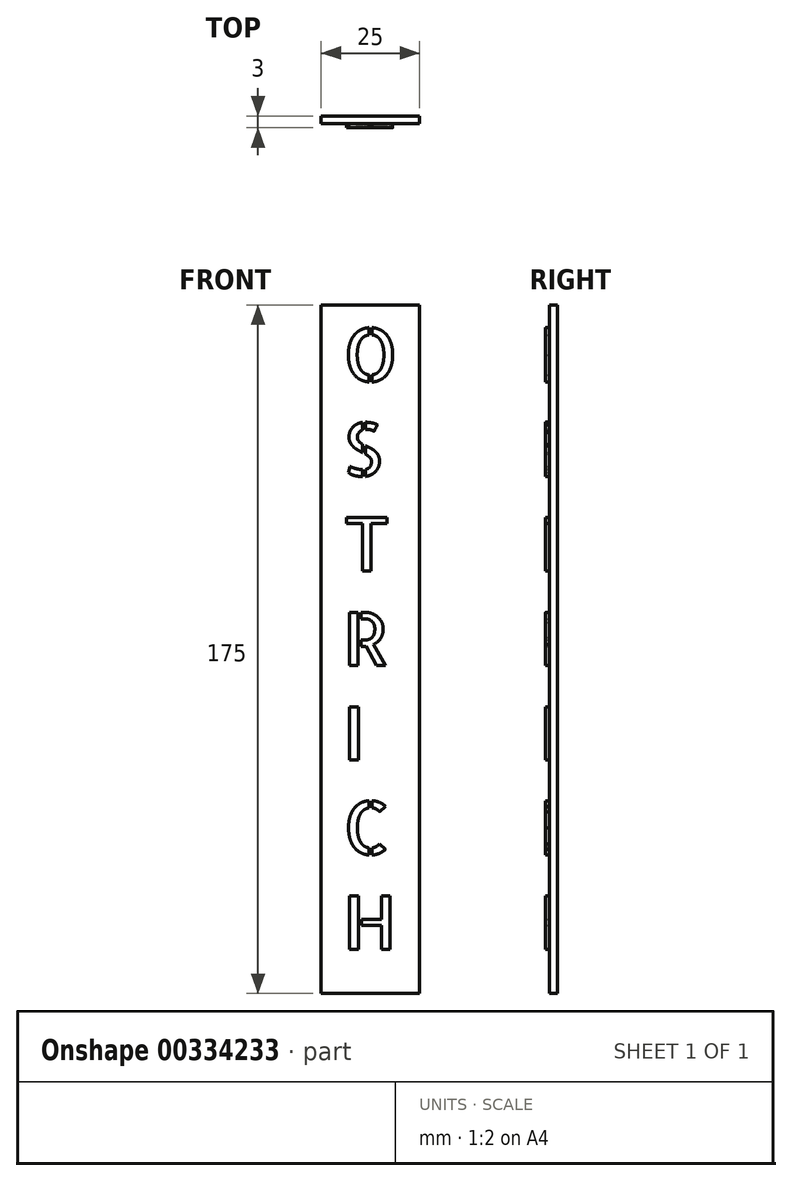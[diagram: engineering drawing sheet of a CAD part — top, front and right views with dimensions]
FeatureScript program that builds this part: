
annotation { "Feature Type Name" : "Feature", "Feature Type Description" : "" }
export const myFeature = defineFeature(function(context is Context, id is Id, definition is map)
    precondition{}
    {
        {
            var Q0;
            Q0=qCreatedBy(makeId("Front.planeOp"),FACE);
            var sketch = newSketch(context, id + "F0", { "sketchPlane" : qUnion([Q0])});
            skLineSegment(sketch, "E0.bottom", {"start": v(12.5, -87.5) * mm, "end": v(-12.5, -87.5) * mm});
            skLineSegment(sketch, "E0.top", {"start": v(12.5, 87.5) * mm, "end": v(-12.5, 87.5) * mm});
            skLineSegment(sketch, "E0.left", {"start": v(12.5, -87.5) * mm, "end": v(12.5, 87.5) * mm});
            skLineSegment(sketch, "E0.right", {"start": v(-12.5, -87.5) * mm, "end": v(-12.5, 87.5) * mm});
            skPoint(sketch, "E0.middle", {"position": v(0, 0) * mm});
            skSolve(sketch);
        }
        {
            var Q0;
            Q0=makeQuery(id+"F0.imprint","IMPRINT",FACE,{"disambiguationData":[TD([[makeQuery(id+"F0.imprint","IMPRINT",EDGE,{"derivedFrom":sQuery(id+"F0.wireOp",EDGE,"E0.bottom")}),-1.0]])]});
            extrude(context, id + "F1", {"entities" : qUnion([Q0]), "depth" : 2 * mm});
        }
        {
            var Q0;
            Q0=makeQuery(id+"F1.opExtrude","CAP_FACE",FACE,{"disambiguationData":[OSD([sQuery(id+"F0.wireOp",EDGE,"E0.bottom"),sQuery(id+"F0.wireOp",EDGE,"E0.top"),sQuery(id+"F0.wireOp",EDGE,"E0.left"),sQuery(id+"F0.wireOp",EDGE,"E0.right")])],"isStart":false});
            var sketch = newSketch(context, id + "F2", { "sketchPlane" : qUnion([Q0])});
            skText(sketch, "E1", { "text": "O\nS\nT\nR\nI\nC\nH", "fontName": "AllertaStencil-Regular.ttf"});
            const initialGuessF2  = {"E1": [-0.00698, 0.06798, 1, 0, 0.01352]};
            skSetInitialGuess(sketch, initialGuessF2);
            skSolve(sketch);
        }
        {
            var Q0;
            Q0 = qSketchRegion(id + "F2", true);
            extrude(context, id + "F3", {"entities" : qUnion([Q0]), "operationType" : NewBodyOperationType.ADD, "depth" : 1 * mm});
        }
    });
